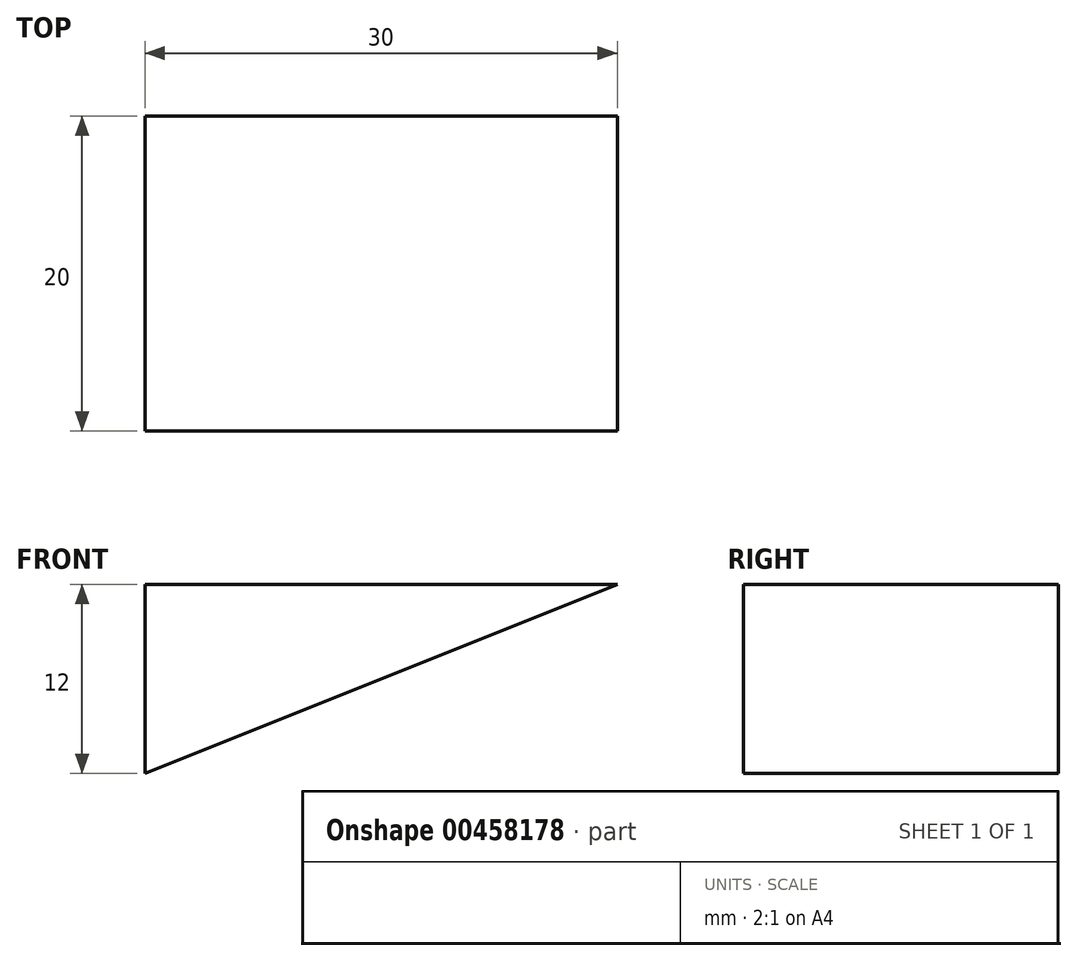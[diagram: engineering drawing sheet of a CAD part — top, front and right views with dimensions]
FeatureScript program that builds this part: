
annotation { "Feature Type Name" : "Feature", "Feature Type Description" : "" }
export const myFeature = defineFeature(function(context is Context, id is Id, definition is map)
    precondition{}
    {
        {
            var Q0;
            Q0=qCreatedBy(makeId("Top.planeOp"),FACE);
            var sketch = newSketch(context, id + "F0", { "sketchPlane" : qUnion([Q0])});
            skLineSegment(sketch, "E0.bottom", {"start": v(-106.51, 12.92) * mm, "end": v(-76.51, 12.92) * mm});
            skLineSegment(sketch, "E0.top", {"start": v(-106.51, -7.08) * mm, "end": v(-76.51, -7.08) * mm});
            skLineSegment(sketch, "E0.left", {"start": v(-106.51, 12.92) * mm, "end": v(-106.51, -7.08) * mm});
            skLineSegment(sketch, "E0.right", {"start": v(-76.51, 12.92) * mm, "end": v(-76.51, -7.08) * mm});
            skLineSegment(sketch, "E1.bottom", {"start": v(6.37, 12.33) * mm, "end": v(36.37, 12.33) * mm});
            skLineSegment(sketch, "E1.top", {"start": v(6.37, -7.67) * mm, "end": v(36.37, -7.67) * mm});
            skLineSegment(sketch, "E1.left", {"start": v(6.37, 12.33) * mm, "end": v(6.37, -7.67) * mm});
            skLineSegment(sketch, "E1.right", {"start": v(36.37, 12.33) * mm, "end": v(36.37, -7.67) * mm});
            skSolve(sketch);
        }
        {
            var Q0;
            Q0=makeQuery(id+"F0.imprint","IMPRINT",FACE,{"disambiguationData":[TD([[makeQuery(id+"F0.imprint","IMPRINT",EDGE,{"derivedFrom":sQuery(id+"F0.wireOp",EDGE,"E0.bottom")}),-1.0]])]});
            var Q1;
            Q1=makeQuery(id+"F0.imprint","IMPRINT",FACE,{"disambiguationData":[TD([[makeQuery(id+"F0.imprint","IMPRINT",EDGE,{"derivedFrom":sQuery(id+"F0.wireOp",EDGE,"E1.bottom")}),-1.0]])]});
            extrude(context, id + "F1", {"entities" : qUnion([Q0, Q1]), "depth" : 12 * mm});
        }
        {
            var Q0;
            Q0=makeQuery(id+"F1.opExtrude","SWEPT_FACE",FACE,{"disambiguationData":[OSD([sQuery(id+"F0.wireOp",EDGE,"E0.top")])]});
            var sketch = newSketch(context, id + "F2", { "sketchPlane" : qUnion([Q0])});
            skLineSegment(sketch, "E2", {"start": v(-106.51, 0) * mm, "end": v(-76.51, 12) * mm});
            skLineSegment(sketch, "E3", {"start": v(-76.51, 12) * mm, "end": v(-106.51, 12) * mm});
            skLineSegment(sketch, "E4", {"start": v(-106.51, 12) * mm, "end": v(-106.51, 0) * mm});
            skSolve(sketch);
        }
        {
            var Q0;
            Q0 = qSketchRegion(id + "F2", true);
            extrude(context, id + "F3", {"entities" : qUnion([Q0]), "operationType" : NewBodyOperationType.INTERSECT, "oppositeDirection" : true, "depth" : 20 * mm});
        }
    });
